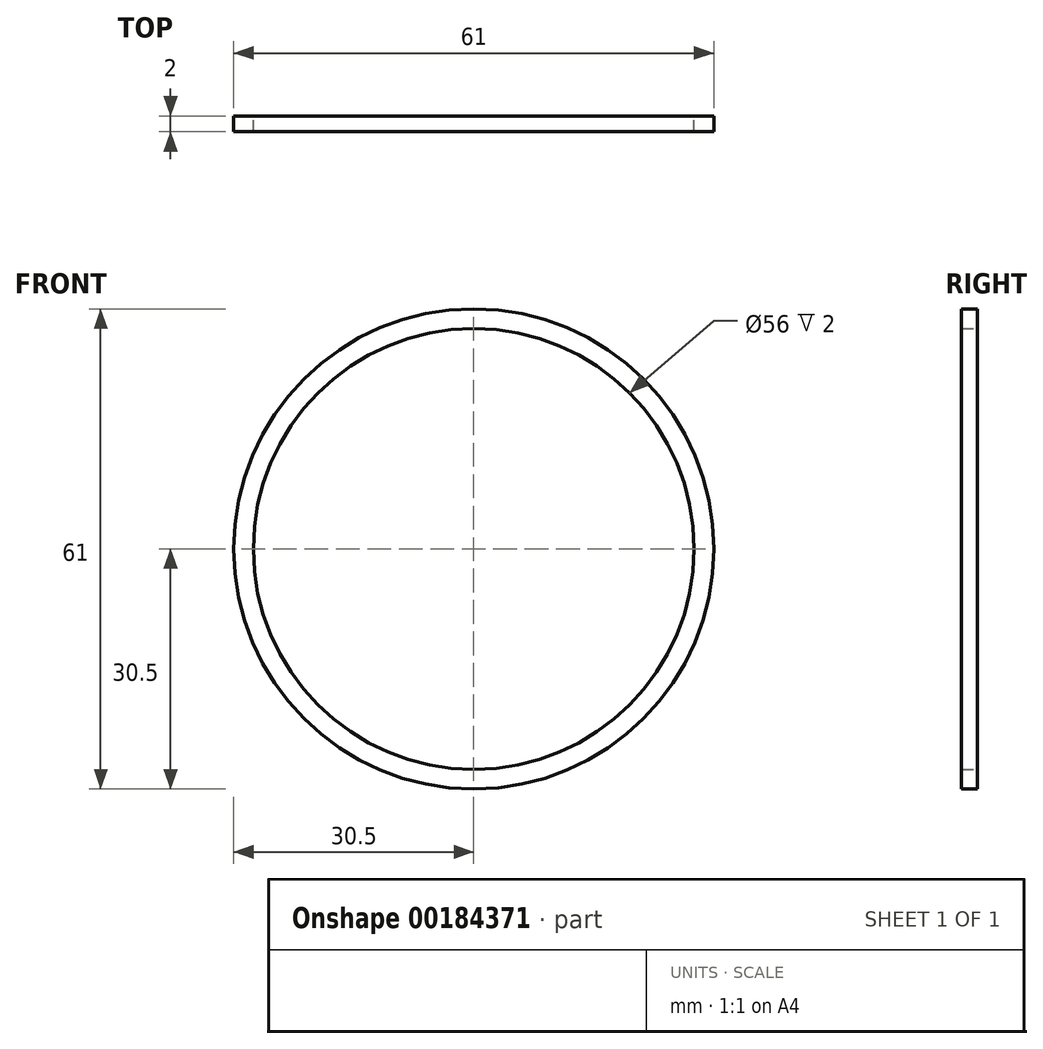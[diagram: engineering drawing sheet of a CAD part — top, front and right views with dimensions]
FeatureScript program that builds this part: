
annotation { "Feature Type Name" : "Feature", "Feature Type Description" : "" }
export const myFeature = defineFeature(function(context is Context, id is Id, definition is map)
    precondition{}
    {
        {
            var Q0;
            Q0=qCreatedBy(makeId("Front.planeOp"),FACE);
            var sketch = newSketch(context, id + "F0", { "sketchPlane" : qUnion([Q0])});
            skCircle(sketch, "E0", {"center": v(0, 0) * mm, "radius": 28 * mm});
            skCircle(sketch, "E1", {"center": v(0, 0) * mm, "radius": 30.5 * mm});
            skSolve(sketch);
        }
        {
            var Q0;
            Q0=makeQuery(id+"F0.imprint","IMPRINT",FACE,{"disambiguationData":[TD([[makeQuery(id+"F0.imprint","IMPRINT",EDGE,{"derivedFrom":sQuery(id+"F0.wireOp",EDGE,"E0")}),-1.0]])]});
            extrude(context, id + "F1", {"entities" : qUnion([Q0]), "depth" : 2 * mm});
        }
    });
